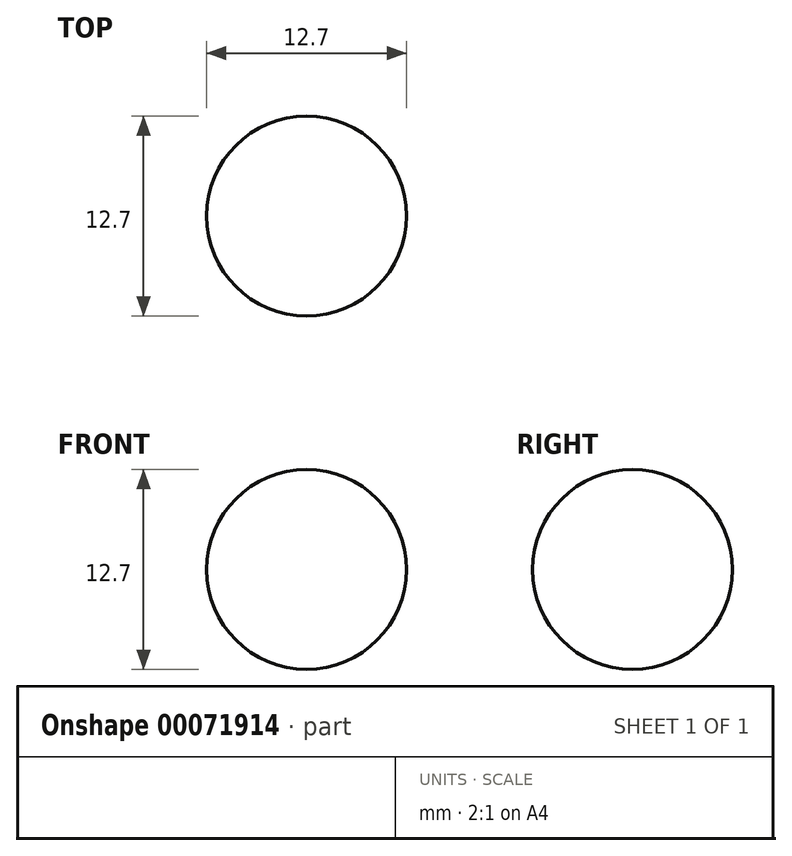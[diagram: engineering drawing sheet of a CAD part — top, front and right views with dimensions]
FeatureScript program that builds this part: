
annotation { "Feature Type Name" : "Feature", "Feature Type Description" : "" }
export const myFeature = defineFeature(function(context is Context, id is Id, definition is map)
    precondition{}
    {
        {
            var Q0;
            Q0=qCreatedBy(makeId("Front.planeOp"),FACE);
            var sketch = newSketch(context, id + "F0", { "sketchPlane" : qUnion([Q0])});
            skLineSegment(sketch, "E0", {"start": v(0, 9.5) * mm, "end": v(0, -10.64) * mm, "construction": true});
            skArc(sketch, "E1", {"start": v(0, 6.35) * mm, "mid": v(6.35, 0) * mm, "end": v(0, -6.35) * mm});
            skSolve(sketch);
        }
        {
            var Q0;
            Q0=sQuery(id+"F0.wireOp",EDGE,"E1");
            var Q1;
            Q1=sQuery(id+"F0.wireOp",EDGE,"E0");
            revolve(context, id + "F1", {"bodyType" : ToolBodyType.SURFACE, "surfaceEntities" : qUnion([Q0]), "axis" : qUnion([Q1]), "revolveType" : RevolveType.FULL});
        }
    });
